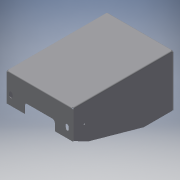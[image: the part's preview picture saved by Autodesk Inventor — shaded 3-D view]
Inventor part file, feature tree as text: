
AUTODESK INVENTOR PART (.ipt)
format: ipt  version: 2016 (Build 200138000, 138)  size: 244,736 bytes
history: native  units: mm
features: sheet_metal_op x14, sketch x11, other x11, reference x4
ambient origin geometry x8: Origin, YZ Plane, XZ Plane, XY Plane, X Axis, Y Axis, Z Axis, Center Point
bodies: Solid1 (feature_tree)
feature tree (40):
  sheet_metal_op  "Face1"
  sheet_metal_op  "Flange1"
  sheet_metal_op  "Flange2"
  sheet_metal_op  "Flange3"
  sketch  "Sketch1"  dims[d0=151.0mm]
  other  "Plate1"
  sketch  "Sketch2"  dims[d1=230.0mm]
  other  "Plate2"
  sheet_metal_op  "Bend1"
  sheet_metal_op  "Corner1"
  sketch  "Sketch3"  dims[d2=1.2mm]
  other  "Plate3"
  sheet_metal_op  "Bend2"
  sheet_metal_op  "Corner2"
  sketch  "Sketch4"  dims[d3=1.2mm]
  other  "Plate4"
  sheet_metal_op  "Bend3"
  sheet_metal_op  "Corner3"
  sketch  "Sketch6"  dims[d4=0.6mm]
  reference  "Reference2"
  sketch  "Sketch8"  dims[d5=2.4mm]
  reference  "Reference3"
  sketch  "Sketch9"  dims[d6=1.2mm]
  sketch  "Sketch10"  dims[d7=75.0mm d8=90.0deg d9=1.2mm]
  reference  "Reference4"
  reference  "Reference5"
  sketch  "Sketch11"  dims[d10=4.8mm]
  sketch  "Sketch12"  dims[d11=1.2mm]
  sketch  "Sketch13"  dims[d12=1.2mm d13=1.2mm d14=0.6mm d15=2.4mm d16=1.2mm d17=120.0mm d18=90.0deg d19=1.2mm d20=4.8mm d21=1.2mm d22=1.2mm d23=1.2mm d24=0.6mm d25=2.4mm d26=1.2mm d27=120.0mm d28=90.0deg d29=1.2mm d30=4.8mm d31=1.2mm d32=1.2mm d33=4.8mm d34=1.2mm d35=1.2mm d36=0.0mm d37=10.0mm d38=4.8mm d39=1.2mm d40=1.2mm d41=0.0mm d42=10.0mm d43=4.8mm d44=1.2mm d45=1.2mm d46=0.0mm d47=10.0mm d48=4.8mm d49=1.2mm d50=1.2mm d51=0.0mm d52=10.0mm d55=1.2mm d56=0.0mm d58=1.2mm d59=0.0mm d60=1.2mm d61=0.0mm d62=4.0mm d63=5.0mm d64=5.0mm d65=4.0mm d66=1.2mm d67=0.0mm d68=8.0mm d69=1.2mm d70=0.0mm d71=33.0mm d72=1.2mm d73=0.0mm d74=70.0mm d75=45.0mm d76=6.0mm d77=1.2mm d78=0.0mm]
  sheet_metal_op  "Corner4"
  sheet_metal_op  "Corner5"
  sheet_metal_op  "Corner6"
  sheet_metal_op  "Corner7"
  other  "Cut2"
  other  "Cut3"
  other  "Cut4"
  other  "Cut5"
  other  "Cut6"
  other  "Cut7"
  other  "Cut8"
